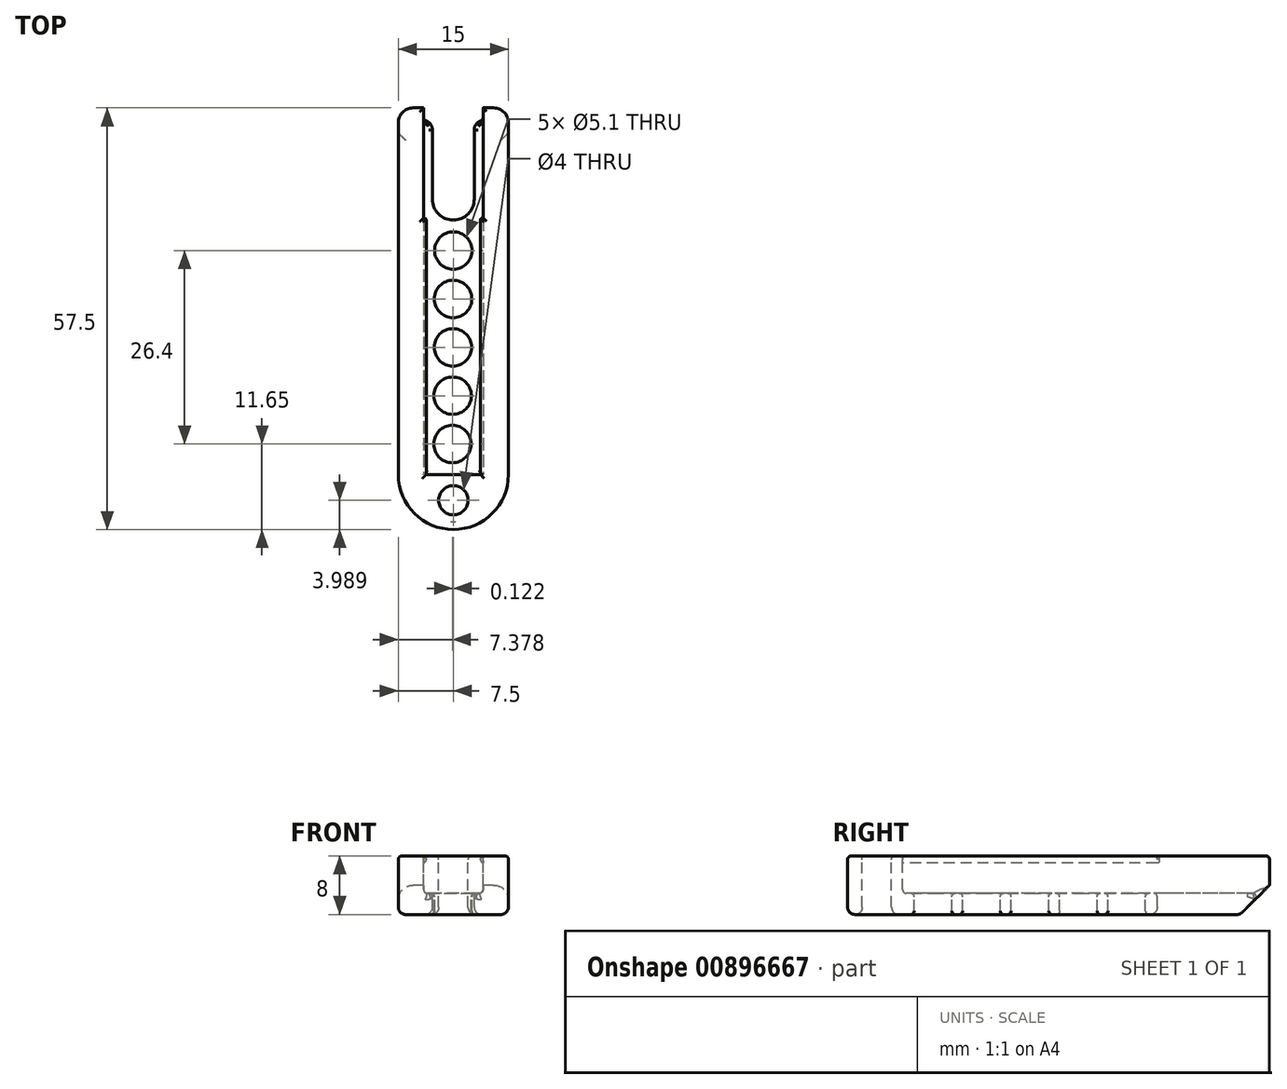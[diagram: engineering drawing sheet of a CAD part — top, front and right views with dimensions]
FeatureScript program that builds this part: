
annotation { "Feature Type Name" : "Feature", "Feature Type Description" : "" }
export const myFeature = defineFeature(function(context is Context, id is Id, definition is map)
    precondition{}
    {
        {
            var Q0;
            Q0=qCreatedBy(makeId("Top.planeOp"),FACE);
            var sketch = newSketch(context, id + "F0", { "sketchPlane" : qUnion([Q0])});
            skLineSegment(sketch, "E0.bottom", {"start": v(-7.5, -25) * mm, "end": v(7.5, -25) * mm});
            skLineSegment(sketch, "E0.top", {"start": v(-7.5, 25) * mm, "end": v(7.5, 25) * mm});
            skLineSegment(sketch, "E0.left", {"start": v(-7.5, -25) * mm, "end": v(-7.5, 25) * mm});
            skLineSegment(sketch, "E0.right", {"start": v(7.5, -25) * mm, "end": v(7.5, 25) * mm});
            skPoint(sketch, "E0.middle", {"position": v(0, 0) * mm});
            skCircle(sketch, "E1", {"center": v(0, -25) * mm, "radius": 7.5 * mm});
            skPoint(sketch, "E2.visualSharp", {"position": v(-7.5, 25) * mm});
            skPoint(sketch, "E3.visualSharp", {"position": v(7.5, 25) * mm});
            skSolve(sketch);
        }
        {
            var Q0;
            Q0=qSketchRegion(id+"F0",true);
            extrude(context, id + "F1", {"entities" : qUnion([Q0]), "depth" : 8 * mm, "offsetDistance" : 25 * mm});
        }
        {
            var Q0;
            Q0=makeQuery(id+"F1.opExtrude","CAP_FACE",FACE,{"disambiguationData":[OSD([sQuery(id+"F0.wireOp",EDGE,"E0.top"),sQuery(id+"F0.wireOp",EDGE,"E0.left"),sQuery(id+"F0.wireOp",EDGE,"E0.right"),sQuery(id+"F0.wireOp",EDGE,"E1")])],"isStart":false});
            var sketch = newSketch(context, id + "F2", { "sketchPlane" : qUnion([Q0])});
            skLineSegment(sketch, "E4.bottom", {"start": v(-4.05, 25) * mm, "end": v(4.05, 25) * mm});
            skLineSegment(sketch, "E4.top", {"start": v(-4.05, -25) * mm, "end": v(4.05, -25) * mm});
            skLineSegment(sketch, "E4.left", {"start": v(-4.05, 25) * mm, "end": v(-4.05, -25) * mm});
            skLineSegment(sketch, "E4.right", {"start": v(4.05, 25) * mm, "end": v(4.05, -25) * mm});
            skPoint(sketch, "E4.middle", {"position": v(0, 0) * mm});
            skCircle(sketch, "E5", {"center": v(0, -28.51) * mm, "radius": 2 * mm});
            skSolve(sketch);
        }
        {
            var Q0;
            Q0=qSketchRegion(id+"F2",true);
            extrude(context, id + "F3", {"entities" : qUnion([Q0]), "operationType" : NewBodyOperationType.REMOVE, "oppositeDirection" : true, "depth" : 5.1 * mm, "offsetDistance" : 25 * mm});
        }
        {
            var Q0;
            Q0=makeQuery(id+"F1.opExtrude","CAP_FACE",FACE,{"disambiguationData":[OSD([sQuery(id+"F0.wireOp",EDGE,"E0.top"),sQuery(id+"F0.wireOp",EDGE,"E0.left"),sQuery(id+"F0.wireOp",EDGE,"E0.right"),sQuery(id+"F0.wireOp",EDGE,"E1")])],"isStart":false});
            var sketch = newSketch(context, id + "F4", { "sketchPlane" : qUnion([Q0])});
            skCircle(sketch, "E6", {"center": v(0, -28.51) * mm, "radius": 2 * mm});
            skSolve(sketch);
        }
        {
            var Q0;
            Q0=qSketchRegion(id+"F4",true);
            extrude(context, id + "F5", {"entities" : qUnion([Q0]), "operationType" : NewBodyOperationType.REMOVE, "oppositeDirection" : true, "depth" : 25 * mm, "offsetDistance" : 25 * mm});
        }
        {
            var Q0;
            Q0=makeQuery(id+"F1.opExtrude","CAP_EDGE",EDGE,{"disambiguationData":[OSD([sQuery(id+"F0.wireOp",EDGE,"E0.top")])],"isStart":true});
            chamfer(context, id + "F6", {"entities" : qUnion([Q0]), "width" : 4 * mm, "tangentPropagation" : true});
        }
        {
            var Q0;
            Q0=makeQuery(id+"F1.opExtrude","SWEPT_EDGE",EDGE,{"disambiguationData":[OSD([sQuery(id+"F0.wireOp",EDGE,"E0.top"),sQuery(id+"F0.wireOp",EDGE,"E0.right")])]});
            var Q1;
            Q1=makeQuery(id+"F1.opExtrude","SWEPT_EDGE",EDGE,{"disambiguationData":[OSD([sQuery(id+"F0.wireOp",EDGE,"E0.top"),sQuery(id+"F0.wireOp",EDGE,"E0.left")])]});
            fillet(context, id + "F7", {"entities" : qUnion([Q0, Q1]), "radius" : 2 * mm, "tangentPropagation" : true, "allowEdgeOverflow" : false});
        }
        {
            var Q0;
            Q0=makeQuery(id+"F3.boolean.opBoolean","COPY",FACE,{"derivedFrom":makeQuery(id+"F3.opExtrude","CAP_FACE",FACE,{"disambiguationData":[OSD([sQuery(id+"F2.wireOp",EDGE,"E4.bottom"),sQuery(id+"F2.wireOp",EDGE,"E4.top"),sQuery(id+"F2.wireOp",EDGE,"E4.left"),sQuery(id+"F2.wireOp",EDGE,"E4.right")])],"isStart":false})});
            var sketch = newSketch(context, id + "F8", { "sketchPlane" : qUnion([Q0])});
            skLineSegment(sketch, "E7.left", {"start": v(-2.85, 24.64) * mm, "end": v(-2.85, 12.55) * mm});
            skLineSegment(sketch, "E7.right", {"start": v(2.85, 24.64) * mm, "end": v(2.85, 12.55) * mm});
            skArc(sketch, "E8", {"start": v(-2.85, 12.55) * mm, "mid": v(0, 9.7) * mm, "end": v(2.85, 12.55) * mm});
            skLineSegment(sketch, "E9", {"start": v(-2.85, 24.64) * mm, "end": v(2.85, 24.64) * mm});
            skSolve(sketch);
        }
        {
            var Q0;
            Q0=qSketchRegion(id+"F8",true);
            extrude(context, id + "F9", {"entities" : qUnion([Q0]), "operationType" : NewBodyOperationType.REMOVE, "oppositeDirection" : true, "depth" : 25 * mm, "offsetDistance" : 25 * mm});
        }
        {
            var Q0;
            Q0=makeQuery(id+"F1.opExtrude","CAP_FACE",FACE,{"disambiguationData":[OSD([sQuery(id+"F0.wireOp",EDGE,"E0.top"),sQuery(id+"F0.wireOp",EDGE,"E0.left"),sQuery(id+"F0.wireOp",EDGE,"E0.right"),sQuery(id+"F0.wireOp",EDGE,"E1")])],"isStart":true});
            var Q1;
            Q1=makeQuery(id+"F9.boolean.opBoolean","INTERSECT",EDGE,{"derivedFrom":[makeQuery(id+"F6.opChamfer","BLEND_FACE",FACE,{"disambiguationData":[OSD([sQuery(id+"F0.wireOp",EDGE,"E0.top")])]}),makeQuery(id+"F9.opExtrude","SWEPT_FACE",FACE,{"disambiguationData":[OSD([sQuery(id+"F8.wireOp",EDGE,"E7.left")])]})]});
            var Q2;
            Q2=makeQuery(id+"F9.boolean.opBoolean","INTERSECT",EDGE,{"derivedFrom":[makeQuery(id+"F6.opChamfer","BLEND_FACE",FACE,{"disambiguationData":[OSD([sQuery(id+"F0.wireOp",EDGE,"E0.top")])]}),makeQuery(id+"F9.opExtrude","SWEPT_FACE",FACE,{"disambiguationData":[OSD([sQuery(id+"F8.wireOp",EDGE,"E7.right")])]})]});
            fillet(context, id + "F10", {"entities" : qUnion([Q0, Q1, Q2]), "radius" : 1 * mm, "tangentPropagation" : true, "allowEdgeOverflow" : false});
        }
        {
            var Q0;
            Q0=makeQuery(id+"F3.boolean.opBoolean","COPY",FACE,{"derivedFrom":makeQuery(id+"F3.opExtrude","SWEPT_FACE",FACE,{"disambiguationData":[OSD([sQuery(id+"F2.wireOp",EDGE,"E4.top")])]})});
            var sketch = newSketch(context, id + "F11", { "sketchPlane" : qUnion([Q0])});
            skLineSegment(sketch, "E10", {"start": v(-4.05, 8) * mm, "end": v(-2.55, 8) * mm});
            skLineSegment(sketch, "E11", {"start": v(-2.55, 8) * mm, "end": v(-4.05, 7) * mm});
            skLineSegment(sketch, "E12", {"start": v(-4.05, 7) * mm, "end": v(-4.05, 8) * mm});
            skLineSegment(sketch, "E13.MirrorCS", {"start": v(4.05, 7) * mm, "end": v(4.05, 8) * mm});
            skLineSegment(sketch, "E14.MirrorCS", {"start": v(2.55, 8) * mm, "end": v(4.05, 7) * mm});
            skLineSegment(sketch, "E15.MirrorCS", {"start": v(4.05, 8) * mm, "end": v(2.55, 8) * mm});
            skSolve(sketch);
        }
        {
            var Q0;
            Q0=qSketchRegion(id+"F11",true);
            extrude(context, id + "F12", {"entities" : qUnion([Q0]), "operationType" : NewBodyOperationType.ADD, "depth" : 35 * mm, "offsetDistance" : 25 * mm});
        }
        {
            var Q0;
            Q0=makeQuery(id+"F3.boolean.opBoolean","COPY",FACE,{"derivedFrom":makeQuery(id+"F3.opExtrude","CAP_FACE",FACE,{"disambiguationData":[OSD([sQuery(id+"F2.wireOp",EDGE,"E4.bottom"),sQuery(id+"F2.wireOp",EDGE,"E4.top"),sQuery(id+"F2.wireOp",EDGE,"E4.left"),sQuery(id+"F2.wireOp",EDGE,"E4.right")])],"isStart":false})});
            var sketch = newSketch(context, id + "F13", { "sketchPlane" : qUnion([Q0])});
            skCircle(sketch, "E16", {"center": v(0, 5.55) * mm, "radius": 2.55 * mm});
            skCircle(sketch, "E17.1.0.0", {"center": v(-0.03, -1.05) * mm, "radius": 2.55 * mm});
            skCircle(sketch, "E17.2.0.0", {"center": v(-0.06, -7.65) * mm, "radius": 2.55 * mm});
            skCircle(sketch, "E17.3.0.0", {"center": v(-0.1, -14.25) * mm, "radius": 2.55 * mm});
            skCircle(sketch, "E17.4.0.0", {"center": v(-0.12, -20.85) * mm, "radius": 2.55 * mm});
            skLineSegment(sketch, "E17.direction1", {"start": v(0, 5.55) * mm, "end": v(-0.03, -1.05) * mm, "construction": true});
            skSolve(sketch);
        }
        {
            var Q0;
            Q0=qSketchRegion(id+"F13",true);
            extrude(context, id + "F14", {"entities" : qUnion([Q0]), "operationType" : NewBodyOperationType.REMOVE, "oppositeDirection" : true, "depth" : 25 * mm, "offsetDistance" : 25 * mm});
        }
        {
            var Q0;
            Q0=makeQuery(id+"F12.boolean.opBoolean","MERGE",FACE,{"derivedFrom":[makeQuery(id+"F1.opExtrude","CAP_FACE",FACE,{"disambiguationData":[OSD([sQuery(id+"F0.wireOp",EDGE,"E0.top"),sQuery(id+"F0.wireOp",EDGE,"E0.left"),sQuery(id+"F0.wireOp",EDGE,"E0.right"),sQuery(id+"F0.wireOp",EDGE,"E1")])],"isStart":false}),makeQuery(id+"F12.opExtrude","SWEPT_FACE",FACE,{"disambiguationData":[OSD([sQuery(id+"F11.wireOp",EDGE,"E10")])]}),makeQuery(id+"F12.opExtrude","SWEPT_FACE",FACE,{"disambiguationData":[OSD([sQuery(id+"F11.wireOp",EDGE,"E15.MirrorCS")])]})]});
            var Q1;
            Q1=makeQuery(id+"F3.boolean.opBoolean","COPY",FACE,{"derivedFrom":makeQuery(id+"F3.opExtrude","CAP_FACE",FACE,{"disambiguationData":[OSD([sQuery(id+"F2.wireOp",EDGE,"E4.bottom"),sQuery(id+"F2.wireOp",EDGE,"E4.top"),sQuery(id+"F2.wireOp",EDGE,"E4.left"),sQuery(id+"F2.wireOp",EDGE,"E4.right")])],"isStart":false})});
            var Q2;
            Q2=makeQuery(id+"F3.boolean.opBoolean","COPY",EDGE,{"derivedFrom":makeQuery(id+"F3.opExtrude","SWEPT_EDGE",EDGE,{"disambiguationData":[OSD([sQuery(id+"F0.wireOp",EDGE,"E0.top"),sQuery(id+"F2.wireOp",EDGE,"E4.bottom"),sQuery(id+"F2.wireOp",EDGE,"E4.left")])]})});
            var Q3;
            Q3=makeQuery(id+"F3.boolean.opBoolean","COPY",EDGE,{"derivedFrom":makeQuery(id+"F3.opExtrude","SWEPT_EDGE",EDGE,{"disambiguationData":[OSD([sQuery(id+"F0.wireOp",EDGE,"E0.top"),sQuery(id+"F2.wireOp",EDGE,"E4.bottom"),sQuery(id+"F2.wireOp",EDGE,"E4.right")])]})});
            fillet(context, id + "F15", {"entities" : qUnion([Q0, Q1, Q2, Q3]), "radius" : 0.5 * mm, "tangentPropagation" : true, "allowEdgeOverflow" : false});
        }
        {
            var Q0;
            Q0=makeQuery(id+"F14.boolean.opBoolean","INTERSECT",EDGE,{"derivedFrom":[makeQuery(id+"F1.opExtrude","CAP_FACE",FACE,{"disambiguationData":[OSD([sQuery(id+"F0.wireOp",EDGE,"E0.top"),sQuery(id+"F0.wireOp",EDGE,"E0.left"),sQuery(id+"F0.wireOp",EDGE,"E0.right"),sQuery(id+"F0.wireOp",EDGE,"E1")])],"isStart":true}),makeQuery(id+"F14.opExtrude","SWEPT_FACE",FACE,{"disambiguationData":[OSD([sQuery(id+"F13.wireOp",EDGE,"E16")])]})]});
            var Q1;
            Q1=makeQuery(id+"F14.boolean.opBoolean","INTERSECT",EDGE,{"derivedFrom":[makeQuery(id+"F1.opExtrude","CAP_FACE",FACE,{"disambiguationData":[OSD([sQuery(id+"F0.wireOp",EDGE,"E0.top"),sQuery(id+"F0.wireOp",EDGE,"E0.left"),sQuery(id+"F0.wireOp",EDGE,"E0.right"),sQuery(id+"F0.wireOp",EDGE,"E1")])],"isStart":true}),makeQuery(id+"F14.opExtrude","SWEPT_FACE",FACE,{"disambiguationData":[OSD([sQuery(id+"F13.wireOp",EDGE,"E17.1.0.0")])]})]});
            var Q2;
            Q2=makeQuery(id+"F14.boolean.opBoolean","INTERSECT",EDGE,{"derivedFrom":[makeQuery(id+"F1.opExtrude","CAP_FACE",FACE,{"disambiguationData":[OSD([sQuery(id+"F0.wireOp",EDGE,"E0.top"),sQuery(id+"F0.wireOp",EDGE,"E0.left"),sQuery(id+"F0.wireOp",EDGE,"E0.right"),sQuery(id+"F0.wireOp",EDGE,"E1")])],"isStart":true}),makeQuery(id+"F14.opExtrude","SWEPT_FACE",FACE,{"disambiguationData":[OSD([sQuery(id+"F13.wireOp",EDGE,"E17.2.0.0")])]})]});
            var Q3;
            Q3=makeQuery(id+"F14.boolean.opBoolean","INTERSECT",EDGE,{"derivedFrom":[makeQuery(id+"F1.opExtrude","CAP_FACE",FACE,{"disambiguationData":[OSD([sQuery(id+"F0.wireOp",EDGE,"E0.top"),sQuery(id+"F0.wireOp",EDGE,"E0.left"),sQuery(id+"F0.wireOp",EDGE,"E0.right"),sQuery(id+"F0.wireOp",EDGE,"E1")])],"isStart":true}),makeQuery(id+"F14.opExtrude","SWEPT_FACE",FACE,{"disambiguationData":[OSD([sQuery(id+"F13.wireOp",EDGE,"E17.3.0.0")])]})]});
            var Q4;
            Q4=makeQuery(id+"F14.boolean.opBoolean","INTERSECT",EDGE,{"derivedFrom":[makeQuery(id+"F1.opExtrude","CAP_FACE",FACE,{"disambiguationData":[OSD([sQuery(id+"F0.wireOp",EDGE,"E0.top"),sQuery(id+"F0.wireOp",EDGE,"E0.left"),sQuery(id+"F0.wireOp",EDGE,"E0.right"),sQuery(id+"F0.wireOp",EDGE,"E1")])],"isStart":true}),makeQuery(id+"F14.opExtrude","SWEPT_FACE",FACE,{"disambiguationData":[OSD([sQuery(id+"F13.wireOp",EDGE,"E17.4.0.0")])]})]});
            fillet(context, id + "F16", {"entities" : qUnion([Q0, Q1, Q2, Q3, Q4]), "radius" : 0.5 * mm, "tangentPropagation" : true, "allowEdgeOverflow" : false});
        }
        {
            var Q0;
            {var subQ0=sQuery(id+"F11.wireOp",EDGE,"E15.MirrorCS");Q0=makeQuery(id+"F15.opFillet","BLEND_EDGE",EDGE,{"blendedFrom":[makeQuery(id+"F12.opExtrude","SWEPT_EDGE",EDGE,{"disambiguationData":[OSD([sQuery(id+"F2.wireOp",EDGE,"E4.top"),sQuery(id+"F11.wireOp",EDGE,"E14.MirrorCS"),subQ0])]}),makeQuery(id+"F12.opExtrude","CAP_EDGE",EDGE,{"disambiguationData":[OSD([subQ0])],"isStart":false})],"blendedInto":[]});}
            var Q1;
            {var subQ0=sQuery(id+"F11.wireOp",EDGE,"E10");Q1=makeQuery(id+"F15.opFillet","BLEND_EDGE",EDGE,{"blendedFrom":[makeQuery(id+"F12.opExtrude","SWEPT_EDGE",EDGE,{"disambiguationData":[OSD([sQuery(id+"F2.wireOp",EDGE,"E4.top"),subQ0,sQuery(id+"F11.wireOp",EDGE,"E11")])]}),makeQuery(id+"F12.opExtrude","CAP_EDGE",EDGE,{"disambiguationData":[OSD([subQ0])],"isStart":false})],"blendedInto":[]});}
            fillet(context, id + "F17", {"entities" : qUnion([Q0, Q1]), "radius" : 0.3 * mm, "tangentPropagation" : true, "allowEdgeOverflow" : false});
        }
    });
